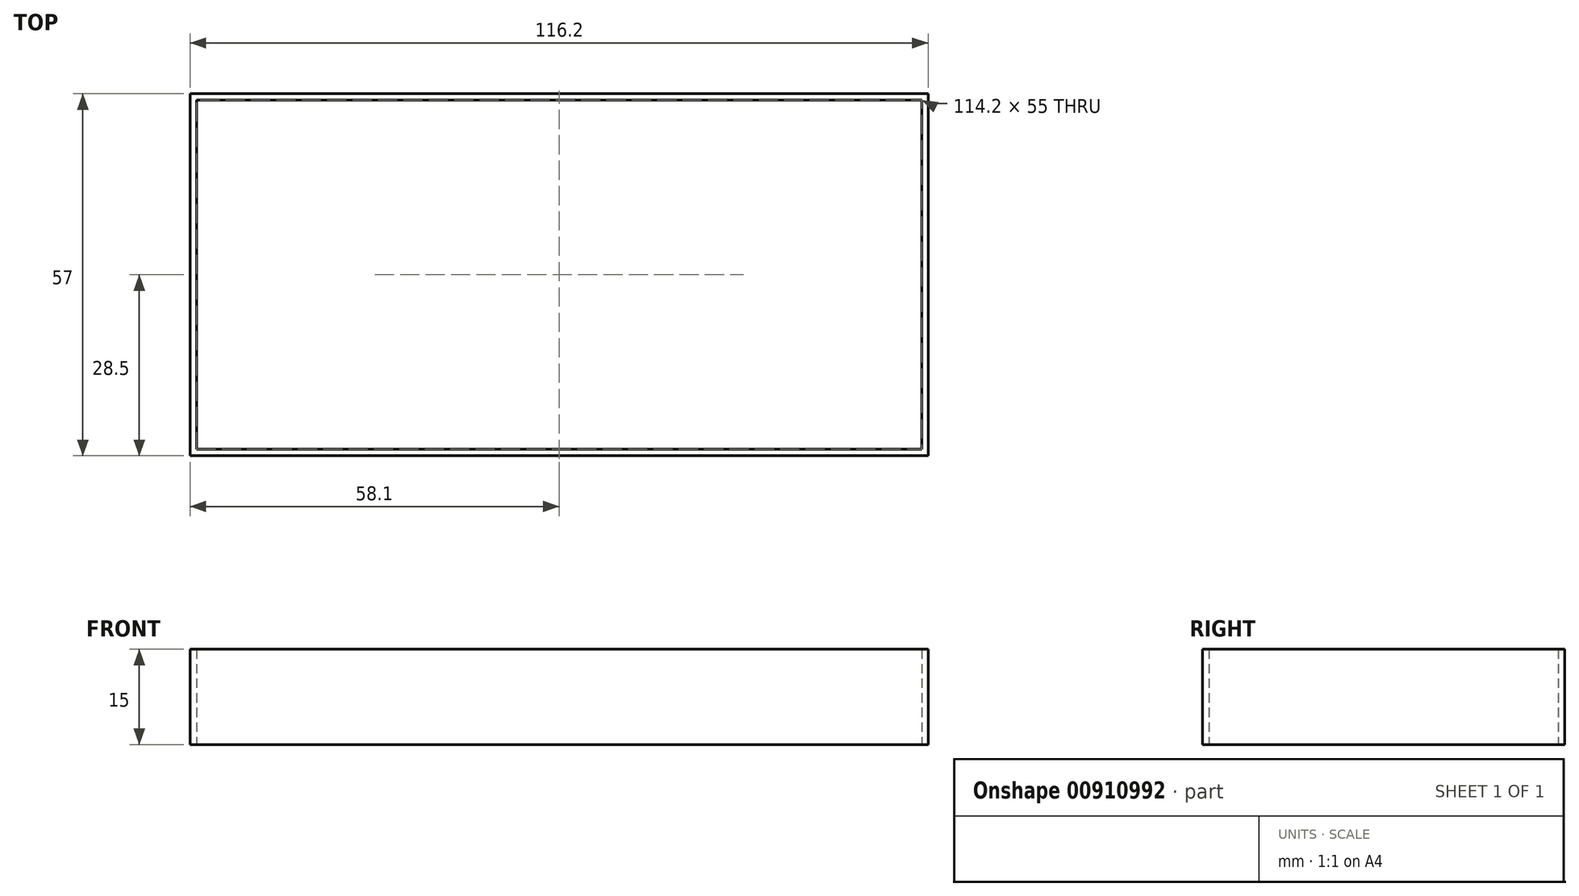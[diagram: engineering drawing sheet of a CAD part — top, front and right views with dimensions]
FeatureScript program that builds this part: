
annotation { "Feature Type Name" : "Feature", "Feature Type Description" : "" }
export const myFeature = defineFeature(function(context is Context, id is Id, definition is map)
    precondition{}
    {
        {
            var Q0;
            Q0=qCreatedBy(makeId("Top.planeOp"),FACE);
            var sketch = newSketch(context, id + "F0", { "sketchPlane" : qUnion([Q0])});
            skLineSegment(sketch, "E0.bottom", {"start": v(0, 0) * mm, "end": v(116.2, 0) * mm});
            skLineSegment(sketch, "E0.top", {"start": v(0, -57) * mm, "end": v(116.2, -57) * mm});
            skLineSegment(sketch, "E0.left", {"start": v(0, 0) * mm, "end": v(0, -57) * mm});
            skLineSegment(sketch, "E0.right", {"start": v(116.2, 0) * mm, "end": v(116.2, -57) * mm});
            skSolve(sketch);
        }
        {
            var Q0;
            Q0 = qSketchRegion(id + "F0", true);
            extrude(context, id + "F1", {"entities" : qUnion([Q0]), "depth" : 15 * mm, "offsetDistance" : 25 * mm});
        }
        {
            var Q0;
            Q0=makeQuery(id+"F1.opExtrude","CAP_FACE",FACE,{"disambiguationData":[OSD([sQuery(id+"F0.wireOp",EDGE,"E0.bottom"),sQuery(id+"F0.wireOp",EDGE,"E0.top"),sQuery(id+"F0.wireOp",EDGE,"E0.left"),sQuery(id+"F0.wireOp",EDGE,"E0.right")])],"isStart":false});
            shell(context, id + "F2", {"entities" : qUnion([Q0]), "thickness" : 1 * mm});
        }
        {
            var Q0;
            Q0=makeQuery(id+"F2.opShell","OFFSET_FACE",FACE,{"disambiguationData":[OSD([sQuery(id+"F0.wireOp",EDGE,"E0.bottom"),sQuery(id+"F0.wireOp",EDGE,"E0.top"),sQuery(id+"F0.wireOp",EDGE,"E0.left"),sQuery(id+"F0.wireOp",EDGE,"E0.right")])]});
            extrude(context, id + "F3", {"entities" : qUnion([Q0]), "operationType" : NewBodyOperationType.REMOVE, "endBound" : BoundingType.THROUGH_ALL, "oppositeDirection" : true, "depth" : 25 * mm, "offsetDistance" : 25 * mm});
        }
    });
